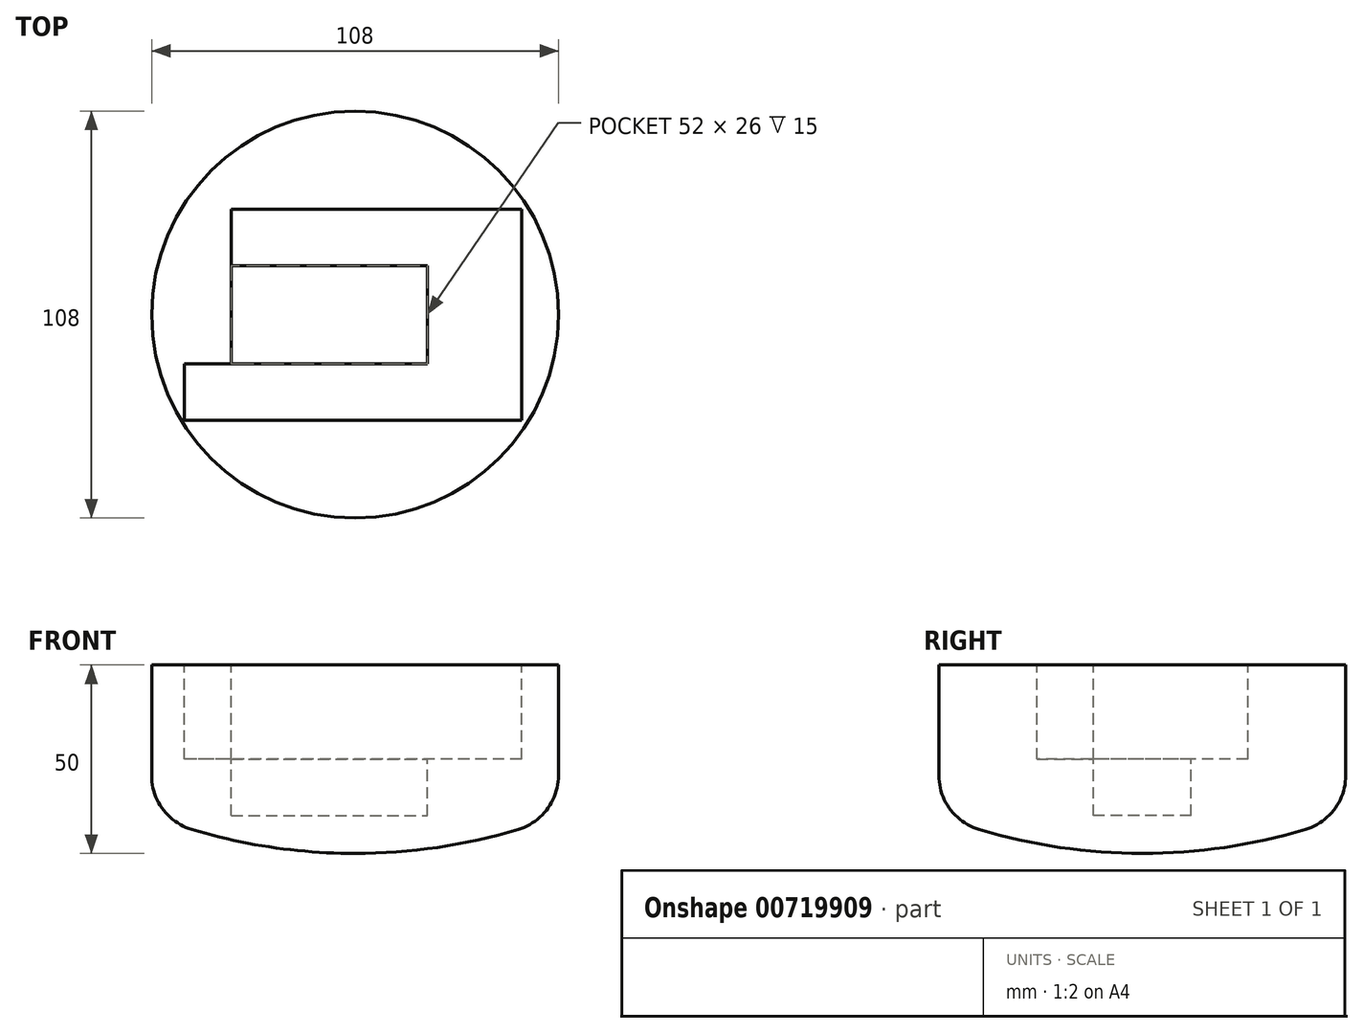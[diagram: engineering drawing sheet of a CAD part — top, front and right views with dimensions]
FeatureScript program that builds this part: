
annotation { "Feature Type Name" : "Feature", "Feature Type Description" : "" }
export const myFeature = defineFeature(function(context is Context, id is Id, definition is map)
    precondition{}
    {
        {
            var Q0;
            Q0=qCreatedBy(makeId("Top.planeOp"),FACE);
            var sketch = newSketch(context, id + "F0", { "sketchPlane" : qUnion([Q0])});
            skCircle(sketch, "E0", {"center": v(0, 0) * mm, "radius": 54 * mm});
            skSolve(sketch);
        }
        {
            var Q0;
            Q0 = qSketchRegion(id + "F0", true);
            extrude(context, id + "F1", {"entities" : qUnion([Q0]), "depth" : 40 * mm, "offsetDistance" : 25 * mm});
        }
        {
            var Q0;
            Q0=makeQuery(id+"F1.opExtrude","CAP_FACE",FACE,{"disambiguationData":[OSD([sQuery(id+"F0.wireOp",EDGE,"E0")])],"isStart":false});
            var sketch = newSketch(context, id + "F2", { "sketchPlane" : qUnion([Q0])});
            skPoint(sketch, "E1.middle", {"position": v(0, 0) * mm});
            skLineSegment(sketch, "E2", {"start": v(46.17, 28) * mm, "end": v(46.17, -28) * mm, "construction": true});
            skLineSegment(sketch, "E3", {"start": v(46.17, 28) * mm, "end": v(44.17, 28) * mm, "construction": true});
            skLineSegment(sketch, "E4.bottom", {"start": v(44.17, 28) * mm, "end": v(-32.83, 28) * mm});
            skLineSegment(sketch, "E4.top", {"start": v(44.17, -28) * mm, "end": v(-32.83, -28) * mm});
            skLineSegment(sketch, "E4.left", {"start": v(44.17, 28) * mm, "end": v(44.17, -28) * mm});
            skLineSegment(sketch, "E4.right", {"start": v(-32.83, 28) * mm, "end": v(-32.83, -28) * mm});
            skLineSegment(sketch, "E5.bottom", {"start": v(-32.83, -28) * mm, "end": v(-45.33, -28) * mm});
            skLineSegment(sketch, "E5.top", {"start": v(-32.83, -13) * mm, "end": v(-45.33, -13) * mm});
            skLineSegment(sketch, "E5.left", {"start": v(-32.83, -28) * mm, "end": v(-32.83, -13) * mm});
            skLineSegment(sketch, "E5.right", {"start": v(-45.33, -28) * mm, "end": v(-45.33, -13) * mm});
            skSolve(sketch);
        }
        {
            var Q0;
            Q0 = qSketchRegion(id + "F2", true);
            extrude(context, id + "F3", {"entities" : qUnion([Q0]), "operationType" : NewBodyOperationType.REMOVE, "oppositeDirection" : true, "depth" : 25 * mm, "offsetDistance" : 25 * mm});
        }
        {
            var Q0;
            Q0=makeQuery(id+"F3.boolean.opBoolean","COPY",FACE,{"derivedFrom":makeQuery(id+"F3.opExtrude","CAP_FACE",FACE,{"disambiguationData":[OSD([sQuery(id+"F2.wireOp",EDGE,"E4.bottom"),sQuery(id+"F2.wireOp",EDGE,"E4.top"),sQuery(id+"F2.wireOp",EDGE,"E4.left"),sQuery(id+"F2.wireOp",EDGE,"E4.right"),sQuery(id+"F2.wireOp",EDGE,"E5.bottom"),sQuery(id+"F2.wireOp",EDGE,"E5.top"),sQuery(id+"F2.wireOp",EDGE,"E5.right")])],"isStart":false})});
            var sketch = newSketch(context, id + "F4", { "sketchPlane" : qUnion([Q0])});
            skLineSegment(sketch, "E6", {"start": v(-32.83, 0) * mm, "end": v(-32.83, 13) * mm});
            skLineSegment(sketch, "E7", {"start": v(-32.83, 13) * mm, "end": v(19.17, 13) * mm});
            skLineSegment(sketch, "E8", {"start": v(19.17, 13) * mm, "end": v(19.17, -13) * mm});
            skLineSegment(sketch, "E9", {"start": v(19.17, -13) * mm, "end": v(-32.83, -13) * mm});
            skLineSegment(sketch, "E10", {"start": v(-32.83, -13) * mm, "end": v(-32.83, 0) * mm});
            skSolve(sketch);
        }
        {
            var Q0;
            Q0 = qSketchRegion(id + "F4", true);
            extrude(context, id + "F5", {"entities" : qUnion([Q0]), "operationType" : NewBodyOperationType.REMOVE, "oppositeDirection" : true, "depth" : 17 * mm, "offsetDistance" : 25 * mm});
        }
        {
            var Q0;
            Q0=qCreatedBy(makeId("Front.planeOp"),FACE);
            var sketch = newSketch(context, id + "F6", { "sketchPlane" : qUnion([Q0])});
            skLineSegment(sketch, "E11", {"start": v(0, 0) * mm, "end": v(0, -10) * mm, "construction": true});
            skPoint(sketch, "E12", {"position": v(-54, 0) * mm});
            skPoint(sketch, "E13", {"position": v(54, 0) * mm});
            skArc(sketch, "E14", {"start": v(-54, 0) * mm, "mid": v(0, -10) * mm, "end": v(54, 0) * mm});
            skLineSegment(sketch, "E15", {"start": v(0, 0) * mm, "end": v(0, -10) * mm});
            skLineSegment(sketch, "E16", {"start": v(0, 0) * mm, "end": v(54, 0) * mm});
            skSolve(sketch);
        }
        {
            var Q0;
            Q0 = qSketchRegion(id + "F6", true);
            var Q1;
            Q1=sQuery(id+"F6.wireOp",EDGE,"E15");
            revolve(context, id + "F7", {"operationType" : NewBodyOperationType.ADD, "surfaceOperationType" : NewSurfaceOperationType.NEW, "entities" : qUnion([Q0]), "axis" : qUnion([Q1]), "revolveType" : RevolveType.FULL});
        }
        {
            var Q0;
            Q0=makeQuery(id+"F7.boolean.opBoolean","MERGE",EDGE,{"derivedFrom":[makeQuery(id+"F1.opExtrude","CAP_EDGE",EDGE,{"disambiguationData":[OSD([sQuery(id+"F0.wireOp",EDGE,"E0")])],"isStart":true}),makeQuery(id+"F7.opRevolve","SWEPT_EDGE",EDGE,{"disambiguationData":[OSD([sQuery(id+"F6.wireOp",EDGE,"E14"),sQuery(id+"F6.wireOp",EDGE,"E16")])]})]});
            fillet(context, id + "F8", {"entities" : qUnion([Q0]), "radius" : 15 * mm, "tangentPropagation" : true, "allowEdgeOverflow" : false});
        }
    });
